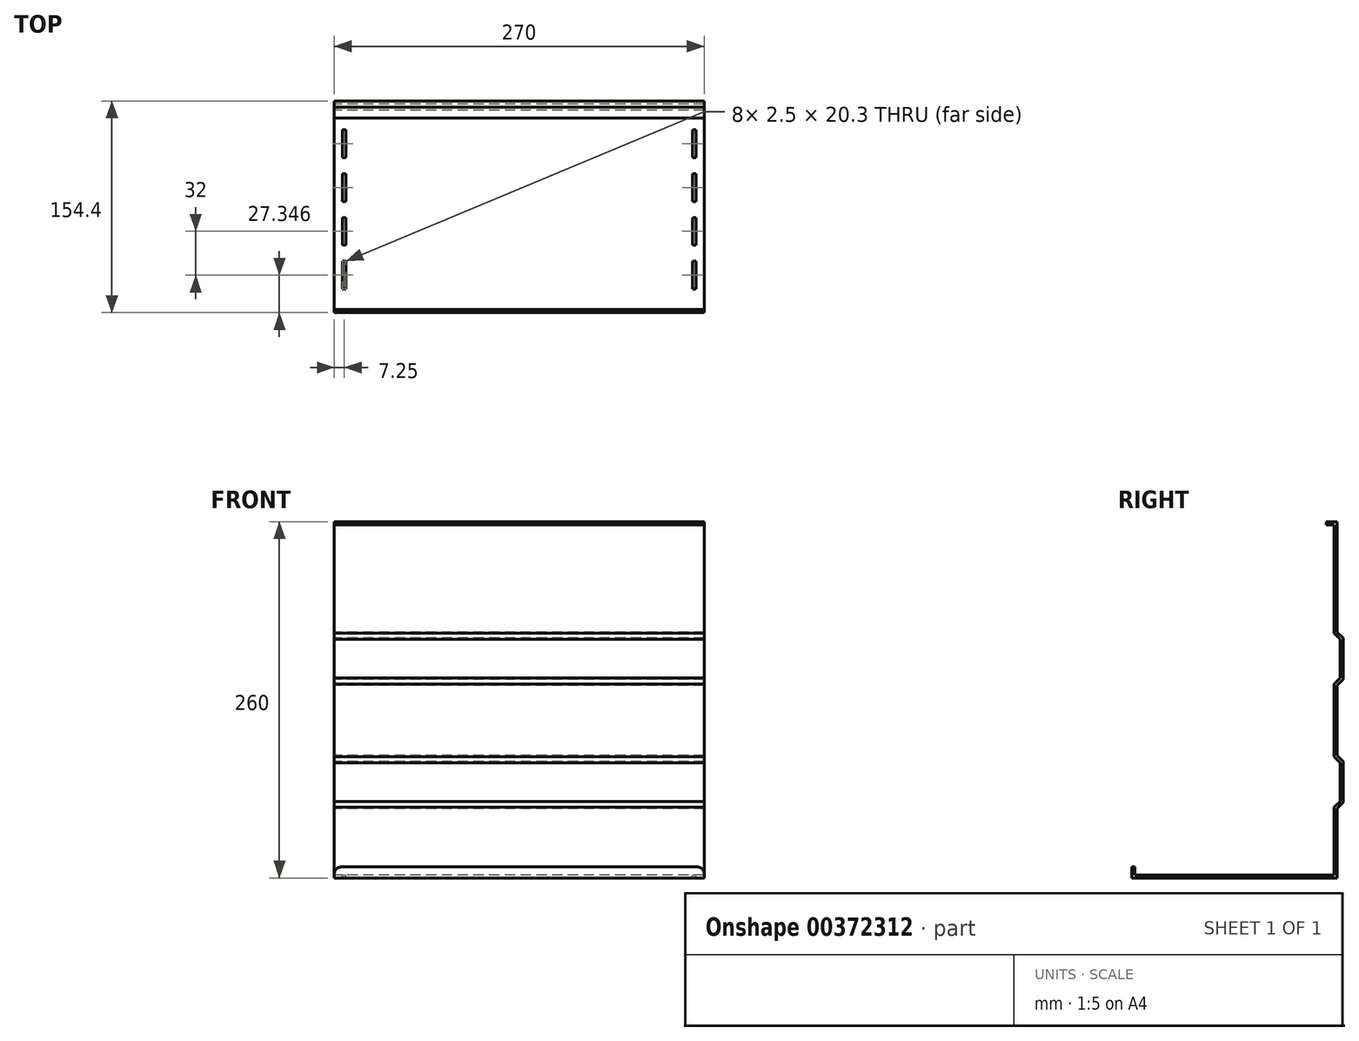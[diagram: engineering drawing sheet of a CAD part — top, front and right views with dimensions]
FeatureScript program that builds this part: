
annotation { "Feature Type Name" : "Feature", "Feature Type Description" : "" }
export const myFeature = defineFeature(function(context is Context, id is Id, definition is map)
    precondition{}
    {
        {
            var Q0;
            Q0=qCreatedBy(makeId("Right.planeOp"),FACE);
            var sketch = newSketch(context, id + "F0", { "sketchPlane" : qUnion([Q0])});
            skLineSegment(sketch, "E0.1", {"start": v(-14.36, 68.13) * mm, "end": v(-14.36, -3.38) * mm});
            skLineSegment(sketch, "E0.2", {"start": v(-9.96, -96.87) * mm, "end": v(-9.96, -126.87) * mm});
            skLineSegment(sketch, "E0.3", {"start": v(-14.36, -40.36) * mm, "end": v(-14.36, -93.38) * mm});
            skLineSegment(sketch, "E0.5", {"start": v(-7.76, -6.87) * mm, "end": v(-7.76, -36.87) * mm});
            skLineSegment(sketch, "E0.6", {"start": v(-12.16, -128.16) * mm, "end": v(-12.16, -181.87) * mm});
            skLineSegment(sketch, "E0.7", {"start": v(-14.36, -130.36) * mm, "end": v(-14.36, -181.58) * mm});
            skLineSegment(sketch, "E0.8", {"start": v(-12.16, -38.16) * mm, "end": v(-12.16, -95.58) * mm});
            skLineSegment(sketch, "E0.10", {"start": v(-7.76, -96.87) * mm, "end": v(-7.76, -126.87) * mm});
            skLineSegment(sketch, "E0.12", {"start": v(-9.96, -6.87) * mm, "end": v(-9.96, -36.87) * mm});
            skLineSegment(sketch, "E0.13", {"start": v(-12.16, 68.13) * mm, "end": v(-12.16, -5.58) * mm});
            skLineSegment(sketch, "E0.14", {"start": v(-12.16, -128.16) * mm, "end": v(-12.16, -131.27) * mm});
            skLineSegment(sketch, "E0.15", {"start": v(-9.96, -96.87) * mm, "end": v(-9.96, -126.87) * mm});
            skLineSegment(sketch, "E0.16", {"start": v(-7.76, -96.87) * mm, "end": v(-7.76, -126.87) * mm});
            skLineSegment(sketch, "E0.19", {"start": v(-9.96, -6.87) * mm, "end": v(-9.96, -36.87) * mm});
            skLineSegment(sketch, "E1.0", {"start": v(-14.36, -130.36) * mm, "end": v(-9.32, -125.32) * mm});
            skLineSegment(sketch, "E2.0", {"start": v(-14.36, -133.47) * mm, "end": v(-7.76, -126.87) * mm});
            skLineSegment(sketch, "E3.0", {"start": v(-7.76, -96.87) * mm, "end": v(-14.36, -90.27) * mm});
            skLineSegment(sketch, "E4.0", {"start": v(-9.32, -98.43) * mm, "end": v(-14.36, -93.38) * mm});
            skLineSegment(sketch, "E5.0", {"start": v(-9.32, -35.32) * mm, "end": v(-14.36, -40.36) * mm});
            skLineSegment(sketch, "E6.0", {"start": v(-7.76, -36.87) * mm, "end": v(-14.36, -43.47) * mm});
            skLineSegment(sketch, "E7.0", {"start": v(-14.36, -0.27) * mm, "end": v(-7.76, -6.87) * mm});
            skLineSegment(sketch, "E8.0", {"start": v(-14.36, -3.38) * mm, "end": v(-9.32, -8.43) * mm});
            skPoint(sketch, "E9.orphan", {"position": v(-14.36, -301.87) * mm});
            skPoint(sketch, "E0.0.start.orphan", {"position": v(-12.16, -301.87) * mm});
            skLineSegment(sketch, "E10.right", {"start": v(-12.16, -179.67) * mm, "end": v(-12.16, -181.87) * mm});
            skLineSegment(sketch, "E11.bottom", {"start": v(-12.16, -181.87) * mm, "end": v(-162.16, -181.87) * mm});
            skLineSegment(sketch, "E11.top", {"start": v(-12.16, -179.67) * mm, "end": v(-162.16, -179.67) * mm});
            skLineSegment(sketch, "E11.left", {"start": v(-12.16, -181.87) * mm, "end": v(-12.16, -179.67) * mm});
            skLineSegment(sketch, "E11.right", {"start": v(-162.16, -181.87) * mm, "end": v(-162.16, -179.67) * mm});
            skLineSegment(sketch, "E12.bottom", {"start": v(-162.16, -181.87) * mm, "end": v(-159.96, -181.87) * mm});
            skLineSegment(sketch, "E12.top", {"start": v(-162.16, -173.87) * mm, "end": v(-159.96, -173.87) * mm});
            skLineSegment(sketch, "E12.left", {"start": v(-162.16, -181.87) * mm, "end": v(-162.16, -173.87) * mm});
            skLineSegment(sketch, "E12.right", {"start": v(-159.96, -181.87) * mm, "end": v(-159.96, -173.87) * mm});
            skLineSegment(sketch, "E13", {"start": v(-12.16, 78.13) * mm, "end": v(-12.16, 68.13) * mm});
            skLineSegment(sketch, "E14", {"start": v(-14.36, 68.13) * mm, "end": v(-14.36, 78.13) * mm});
            skLineSegment(sketch, "E15", {"start": v(-1.7, 68.13) * mm, "end": v(-1.7, 78.13) * mm, "construction": true});
            skLineSegment(sketch, "E16", {"start": v(-1.7, 78.13) * mm, "end": v(-21.46, 78.13) * mm, "construction": true});
            skPoint(sketch, "E16.endSnap0", {"position": v(-14.36, 78.13) * mm});
            skLineSegment(sketch, "E17", {"start": v(-21.46, 78.13) * mm, "end": v(-21.46, 75.93) * mm, "construction": true});
            skLineSegment(sketch, "E18.bottom", {"start": v(-20.16, 78.13) * mm, "end": v(-12.16, 78.13) * mm});
            skLineSegment(sketch, "E18.top", {"start": v(-20.16, 75.93) * mm, "end": v(-12.16, 75.93) * mm});
            skLineSegment(sketch, "E18.left", {"start": v(-20.16, 78.13) * mm, "end": v(-20.16, 75.93) * mm});
            skLineSegment(sketch, "E18.right", {"start": v(-12.16, 78.13) * mm, "end": v(-12.16, 75.93) * mm});
            skSolve(sketch);
        }
        {
            var Q0;
            Q0=qSketchRegion(id+"F0",true);
            extrude(context, id + "F1", {"entities" : qUnion([Q0]), "depth" : 270 * mm});
        }
        {
            var Q0;
            Q0=makeQuery(id+"F1.opExtrude","CAP_EDGE",EDGE,{"disambiguationData":[OSD([sQuery(id+"F0.wireOp",EDGE,"E12.top")])],"isStart":false});
            var Q1;
            Q1=makeQuery(id+"F1.opExtrude","CAP_EDGE",EDGE,{"disambiguationData":[OSD([sQuery(id+"F0.wireOp",EDGE,"E12.top")])],"isStart":true});
            var Q2;
            Q2=makeQuery(id+"FQbqYBv88OOlFCn_5.opExtrude","CAP_EDGE",EDGE,{"disambiguationData":[OSD([sQuery(id+"FkVeNlTqFJrZwbb_5.wireOp",EDGE,"geg2n0oJ-qErj-zygl-pFgj-fnu9iOUp74qN.top")])],"isStart":true});
            var Q3;
            Q3=makeQuery(id+"FQbqYBv88OOlFCn_5.opExtrude","TWEAK_EDGE",EDGE,{"derivedFrom":[makeQuery(id+"F1.opExtrude","CAP_FACE",FACE,{"disambiguationData":[OSD([sQuery(id+"F0.wireOp",EDGE,"E0.1"),sQuery(id+"F0.wireOp",EDGE,"E0.3"),sQuery(id+"F0.wireOp",EDGE,"E0.5"),sQuery(id+"F0.wireOp",EDGE,"E0.6"),sQuery(id+"F0.wireOp",EDGE,"E0.7"),sQuery(id+"F0.wireOp",EDGE,"E0.8"),sQuery(id+"F0.wireOp",EDGE,"E0.15"),sQuery(id+"F0.wireOp",EDGE,"E0.16"),sQuery(id+"F0.wireOp",EDGE,"E0.18"),sQuery(id+"F0.wireOp",EDGE,"E0.19"),sQuery(id+"F0.wireOp",EDGE,"E1.0"),sQuery(id+"F0.wireOp",EDGE,"E2.0"),sQuery(id+"F0.wireOp",EDGE,"E3.0"),sQuery(id+"F0.wireOp",EDGE,"E4.0"),sQuery(id+"F0.wireOp",EDGE,"E5.0"),sQuery(id+"F0.wireOp",EDGE,"E6.0"),sQuery(id+"F0.wireOp",EDGE,"E7.0"),sQuery(id+"F0.wireOp",EDGE,"E8.0"),sQuery(id+"F0.wireOp",EDGE,"38a07ef9-1a91-4555-9129-2b5ad7fe76ca.0"),sQuery(id+"F0.wireOp",EDGE,"4b4fbffe-de69-44bc-863c-3fdb988875ab.0"),sQuery(id+"F0.wireOp",EDGE,"9940175d-dd6f-4403-85d8-10021e686e23.0"),sQuery(id+"F0.wireOp",EDGE,"E11.bottom"),sQuery(id+"F0.wireOp",EDGE,"E11.top"),sQuery(id+"F0.wireOp",EDGE,"E11.left"),sQuery(id+"F0.wireOp",EDGE,"E12.bottom"),sQuery(id+"F0.wireOp",EDGE,"E12.top"),sQuery(id+"F0.wireOp",EDGE,"E12.left"),sQuery(id+"F0.wireOp",EDGE,"E12.right")])],"isStart":true}),makeQuery(id+"FkVeNlTqFJrZwbb_5.imprint","IMPRINT",EDGE,{"derivedFrom":sQuery(id+"FkVeNlTqFJrZwbb_5.wireOp",EDGE,"geg2n0oJ-qErj-zygl-pFgj-fnu9iOUp74qN.top")})]});
            fillet(context, id + "F2", {"entities" : qUnion([Q0, Q1, Q2, Q3]), "radius" : 5 * mm, "tangentPropagation" : true, "allowEdgeOverflow" : false});
        }
        {
            var Q0;
            Q0=makeQuery(id+"F1.opExtrude","SWEPT_FACE",FACE,{"disambiguationData":[OSD([sQuery(id+"F0.wireOp",EDGE,"E11.top")])]});
            var sketch = newSketch(context, id + "F3", { "sketchPlane" : qUnion([Q0])});
            skLineSegment(sketch, "E19.bottom", {"start": v(6, -144.96) * mm, "end": v(8.5, -144.96) * mm});
            skLineSegment(sketch, "E19.top", {"start": v(6, -124.66) * mm, "end": v(8.5, -124.66) * mm});
            skLineSegment(sketch, "E19.left", {"start": v(6, -144.96) * mm, "end": v(6, -124.66) * mm});
            skLineSegment(sketch, "E19.right", {"start": v(8.5, -144.96) * mm, "end": v(8.5, -124.66) * mm});
            skLineSegment(sketch, "E20.0.1.0", {"start": v(8.5, -112.96) * mm, "end": v(8.5, -92.66) * mm});
            skLineSegment(sketch, "E20.0.1.1", {"start": v(6, -112.96) * mm, "end": v(6, -92.66) * mm});
            skLineSegment(sketch, "E20.0.1.2", {"start": v(6, -92.66) * mm, "end": v(8.5, -92.66) * mm});
            skLineSegment(sketch, "E20.0.1.3", {"start": v(6, -112.96) * mm, "end": v(8.5, -112.96) * mm});
            skLineSegment(sketch, "E20.0.2.0", {"start": v(8.5, -80.96) * mm, "end": v(8.5, -60.66) * mm});
            skLineSegment(sketch, "E20.0.2.1", {"start": v(6, -80.96) * mm, "end": v(6, -60.66) * mm});
            skLineSegment(sketch, "E20.0.2.2", {"start": v(6, -60.66) * mm, "end": v(8.5, -60.66) * mm});
            skLineSegment(sketch, "E20.0.2.3", {"start": v(6, -80.96) * mm, "end": v(8.5, -80.96) * mm});
            skLineSegment(sketch, "E20.0.3.0", {"start": v(8.5, -48.96) * mm, "end": v(8.5, -28.66) * mm});
            skLineSegment(sketch, "E20.0.3.1", {"start": v(6, -48.96) * mm, "end": v(6, -28.66) * mm});
            skLineSegment(sketch, "E20.0.3.2", {"start": v(6, -28.66) * mm, "end": v(8.5, -28.66) * mm});
            skLineSegment(sketch, "E20.0.3.3", {"start": v(6, -48.96) * mm, "end": v(8.5, -48.96) * mm});
            skLineSegment(sketch, "E20.1.0.0", {"start": v(264, -144.96) * mm, "end": v(264, -124.66) * mm});
            skLineSegment(sketch, "E20.1.0.1", {"start": v(261.5, -144.96) * mm, "end": v(261.5, -124.66) * mm});
            skLineSegment(sketch, "E20.1.0.2", {"start": v(261.5, -124.66) * mm, "end": v(264, -124.66) * mm});
            skLineSegment(sketch, "E20.1.0.3", {"start": v(261.5, -144.96) * mm, "end": v(264, -144.96) * mm});
            skLineSegment(sketch, "E20.1.1.0", {"start": v(264, -112.96) * mm, "end": v(264, -92.66) * mm});
            skLineSegment(sketch, "E20.1.1.1", {"start": v(261.5, -112.96) * mm, "end": v(261.5, -92.66) * mm});
            skLineSegment(sketch, "E20.1.1.2", {"start": v(261.5, -92.66) * mm, "end": v(264, -92.66) * mm});
            skLineSegment(sketch, "E20.1.1.3", {"start": v(261.5, -112.96) * mm, "end": v(264, -112.96) * mm});
            skLineSegment(sketch, "E20.1.2.0", {"start": v(264, -80.96) * mm, "end": v(264, -60.66) * mm});
            skLineSegment(sketch, "E20.1.2.1", {"start": v(261.5, -80.96) * mm, "end": v(261.5, -60.66) * mm});
            skLineSegment(sketch, "E20.1.2.2", {"start": v(261.5, -60.66) * mm, "end": v(264, -60.66) * mm});
            skLineSegment(sketch, "E20.1.2.3", {"start": v(261.5, -80.96) * mm, "end": v(264, -80.96) * mm});
            skLineSegment(sketch, "E20.1.3.0", {"start": v(264, -48.96) * mm, "end": v(264, -28.66) * mm});
            skLineSegment(sketch, "E20.1.3.1", {"start": v(261.5, -48.96) * mm, "end": v(261.5, -28.66) * mm});
            skLineSegment(sketch, "E20.1.3.2", {"start": v(261.5, -28.66) * mm, "end": v(264, -28.66) * mm});
            skLineSegment(sketch, "E20.1.3.3", {"start": v(261.5, -48.96) * mm, "end": v(264, -48.96) * mm});
            skLineSegment(sketch, "E20.direction1", {"start": v(6, -144.96) * mm, "end": v(261.5, -144.96) * mm, "construction": true});
            skLineSegment(sketch, "E20.direction2", {"start": v(6, -144.96) * mm, "end": v(6, -112.96) * mm, "construction": true});
            skSolve(sketch);
        }
        {
            var Q0;
            Q0 = qSketchRegion(id + "F3", true);
            extrude(context, id + "F4", {"entities" : qUnion([Q0]), "operationType" : NewBodyOperationType.REMOVE, "oppositeDirection" : true, "depth" : 25 * mm, "offsetDistance" : 25 * mm});
        }
    });
